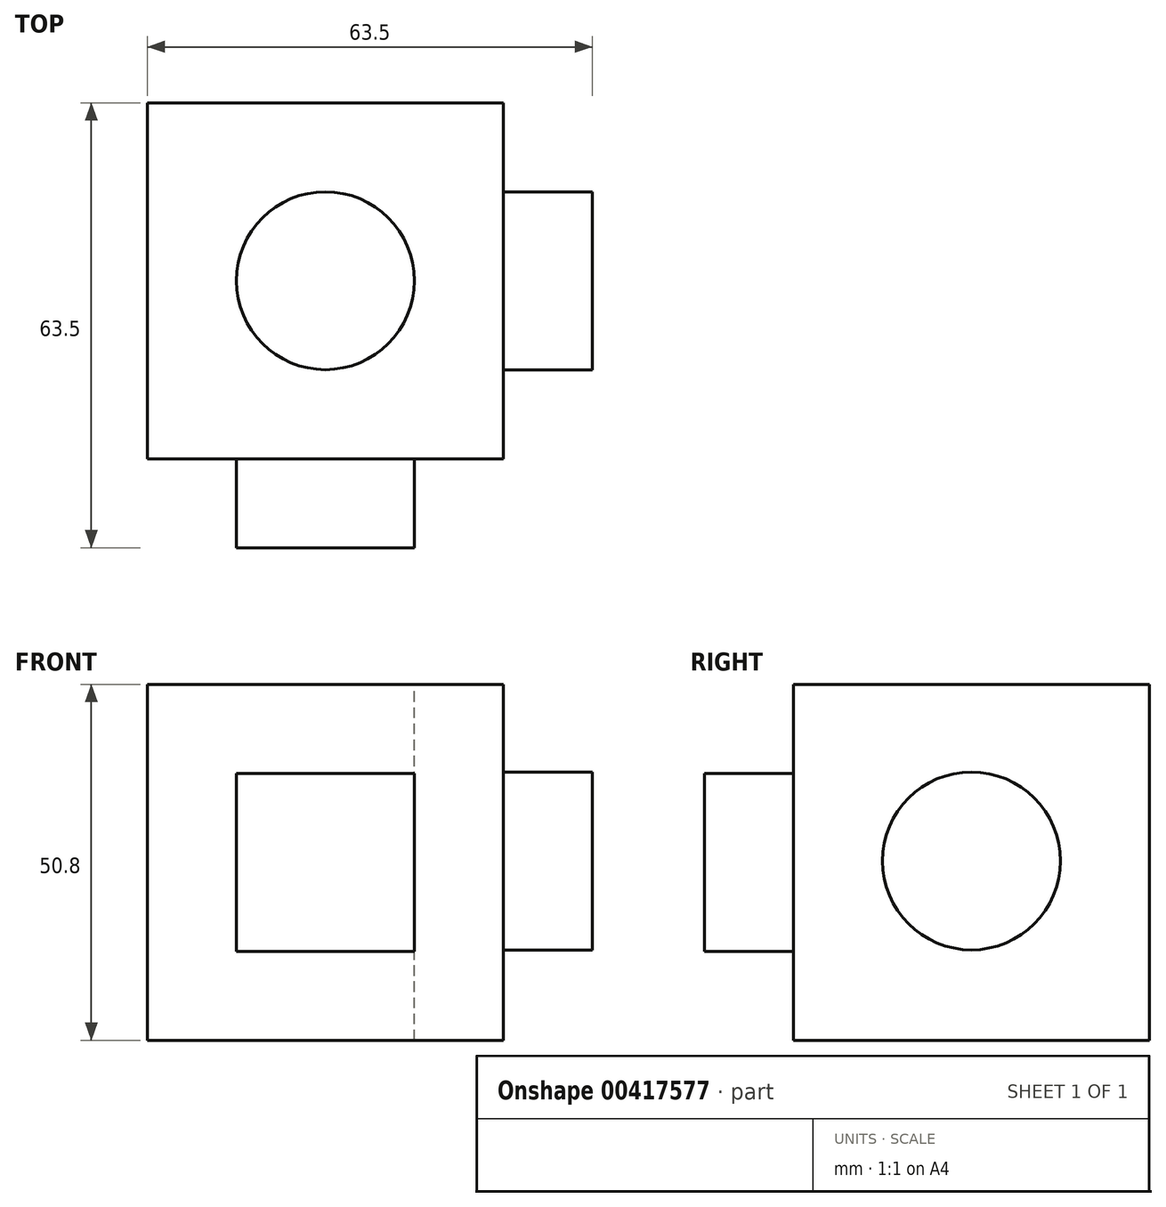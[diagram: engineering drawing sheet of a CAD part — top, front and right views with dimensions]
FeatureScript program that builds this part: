
annotation { "Feature Type Name" : "Feature", "Feature Type Description" : "" }
export const myFeature = defineFeature(function(context is Context, id is Id, definition is map)
    precondition{}
    {
        {
            var Q0;
            Q0=qCreatedBy(makeId("Front.planeOp"),FACE);
            var sketch = newSketch(context, id + "F0", { "sketchPlane" : qUnion([Q0])});
            skLineSegment(sketch, "E0", {"start": v(0, 0) * mm, "end": v(-25.4, 0) * mm});
            skLineSegment(sketch, "E1.left", {"start": v(0, 0) * mm, "end": v(0, 0) * mm});
            skLineSegment(sketch, "E1.right", {"start": v(-25.4, 0) * mm, "end": v(-25.4, 0) * mm});
            skLineSegment(sketch, "E2.bottom", {"start": v(-25.4, 0) * mm, "end": v(25.4, 0) * mm});
            skLineSegment(sketch, "E2.top", {"start": v(-25.4, 50.8) * mm, "end": v(25.4, 50.8) * mm});
            skLineSegment(sketch, "E2.left", {"start": v(-25.4, 0) * mm, "end": v(-25.4, 50.8) * mm});
            skLineSegment(sketch, "E2.right", {"start": v(25.4, 0) * mm, "end": v(25.4, 50.8) * mm});
            skSolve(sketch);
        }
        {
            var Q0;
            Q0=makeQuery(id+"F0.imprint","IMPRINT",FACE,{"disambiguationData":[TD([[makeQuery(id+"F0.imprint","IMPRINT",EDGE,{"derivedFrom":sQuery(id+"F0.wireOp",EDGE,"E2.top")}),-1.0]])]});
            extrude(context, id + "F1", {"entities" : qUnion([Q0]), "depth" : 50.8 * mm});
        }
        {
            var Q0;
            Q0=makeQuery(id+"F1.opExtrude","CAP_FACE",FACE,{"disambiguationData":[OSD([sQuery(id+"F0.wireOp",EDGE,"E2.bottom"),sQuery(id+"F0.wireOp",EDGE,"E2.top"),sQuery(id+"F0.wireOp",EDGE,"E2.left"),sQuery(id+"F0.wireOp",EDGE,"E2.right")])],"isStart":false});
            var sketch = newSketch(context, id + "F2", { "sketchPlane" : qUnion([Q0])});
            skLineSegment(sketch, "E3.bottom", {"start": v(-12.7, 12.7) * mm, "end": v(12.7, 12.7) * mm});
            skLineSegment(sketch, "E3.top", {"start": v(-12.7, 38.1) * mm, "end": v(12.7, 38.1) * mm});
            skLineSegment(sketch, "E3.left", {"start": v(-12.7, 12.7) * mm, "end": v(-12.7, 38.1) * mm});
            skLineSegment(sketch, "E3.right", {"start": v(12.7, 12.7) * mm, "end": v(12.7, 38.1) * mm});
            skPoint(sketch, "E3.middle", {"position": v(0, 25.4) * mm});
            skSolve(sketch);
        }
        {
            var Q0;
            Q0=makeQuery(id+"F2.imprint","IMPRINT",FACE,{"disambiguationData":[TD([[makeQuery(id+"F2.imprint","IMPRINT",EDGE,{"derivedFrom":sQuery(id+"F2.wireOp",EDGE,"E3.bottom")}),1.0]])]});
            extrude(context, id + "F3", {"entities" : qUnion([Q0]), "operationType" : NewBodyOperationType.ADD, "depth" : 12.7 * mm});
        }
        {
            var Q0;
            Q0=makeQuery(id+"F1.opExtrude","SWEPT_FACE",FACE,{"disambiguationData":[OSD([sQuery(id+"F0.wireOp",EDGE,"E2.right")])]});
            var sketch = newSketch(context, id + "F4", { "sketchPlane" : qUnion([Q0])});
            skCircle(sketch, "E4", {"center": v(-25.4, 25.6) * mm, "radius": 12.7 * mm});
            skSolve(sketch);
        }
        {
            var Q0;
            Q0=makeQuery(id+"F4.imprint","IMPRINT",FACE,{"disambiguationData":[TD([[makeQuery(id+"F4.imprint","IMPRINT",EDGE,{"derivedFrom":sQuery(id+"F4.wireOp",EDGE,"E4")}),1.0]])]});
            extrude(context, id + "F5", {"entities" : qUnion([Q0]), "operationType" : NewBodyOperationType.ADD, "depth" : 12.7 * mm});
        }
        {
            var Q0;
            Q0=makeQuery(id+"F1.opExtrude","SWEPT_FACE",FACE,{"disambiguationData":[OSD([sQuery(id+"F0.wireOp",EDGE,"E2.top")])]});
            var sketch = newSketch(context, id + "F6", { "sketchPlane" : qUnion([Q0])});
            skCircle(sketch, "E5", {"center": v(0, -25.4) * mm, "radius": 12.7 * mm});
            skSolve(sketch);
        }
        {
            var Q0;
            Q0=makeQuery(id+"F6.imprint","IMPRINT",FACE,{"disambiguationData":[TD([[makeQuery(id+"F6.imprint","IMPRINT",EDGE,{"derivedFrom":sQuery(id+"F6.wireOp",EDGE,"E5")}),1.0]])]});
            extrude(context, id + "F7", {"entities" : qUnion([Q0]), "operationType" : NewBodyOperationType.REMOVE, "oppositeDirection" : true, "depth" : 50.8 * mm});
        }
    });
